# Revit family: BIM_01-1993-09
name_source: partatom
category: Aparatos sanitarios
units: mm (PartAtom-declared; Revit-internal decimal feet)

## family parameters
Activar corte en vistas = No
Anfitrión = Cara
Compartido = No
Corte con vacíos al cargar = No
Cota de conector redondo = Usar diámetro
Mantener orientación de anotación = No
Número OmniClass = 23.31.11.00
Punto de cálculo de habitación = No
Tipo de pieza = Normal

## types (1)
- 01-1993-09
    Alto = 46 mm  [stored 0.150919 ft]
    Ancho = 75 mm
    Conexiones = Acometida: Rosca Hembra ½” NPT Lavadora:
Rosca Macho ¾” NH
    Conexión AC = Sí
    Conexión AF = Sí
    Conexión de residuos = No
    Conexión de ventilación = No
    Date Modified = 25-08-2025
    Descripción = Llave
    Elevación por defecto = 0 mm  [stored 0 ft]
    Fabricante = Gricol
    Garantia Especifica = 20 Años
    Imagen de tipo = LLAVE LAVADORA CROMADA AZUL.jpg
    Link Ficha Tecnica = https://infotecnica.gricol.com
    Materiales del producto = ABS, Latón, Caucho
    Modelo = 01-1993-09
    Plastico - ABS + Colorante azul = Plastico - ABS + Colorante azul
    Plastico - ABS Cromado = Plastico - ABS Cromado
    Presión Maxima = 125.00 psi
    Presión Mínima = 20.00 psi
    Presión de Estaiildo = 500.00 psi
    Product Name = Llave lavadora plástica cromada manija azul
    Referente Normativo = NTC 1644, ASME A112.18.1 / CSA B125.1
    Resistencia a Corrosión = NTC 1156 Sal Neutral
    Rosca NPS 3/4" = 3/4"
    Rosca NPT 1/2" = 1/2"
    Sitio web = https://www.gricol.com
    Temperaturas de trabajo = DE 5° A 71°
    Tipo de Uso = Domestico
    Torque de Conexioón = 61 Nm
    URL = https://www.gricol.com
    Vida Util = 2000 Ciclos

note: [stored X ft] marks values corroborated as IEEE doubles in the binary element streams (Revit-internal decimal feet)

## geometry (parser evidence)
native form markers: Blend x2, Sweep x5
no freeform markers — native parametric forms only
